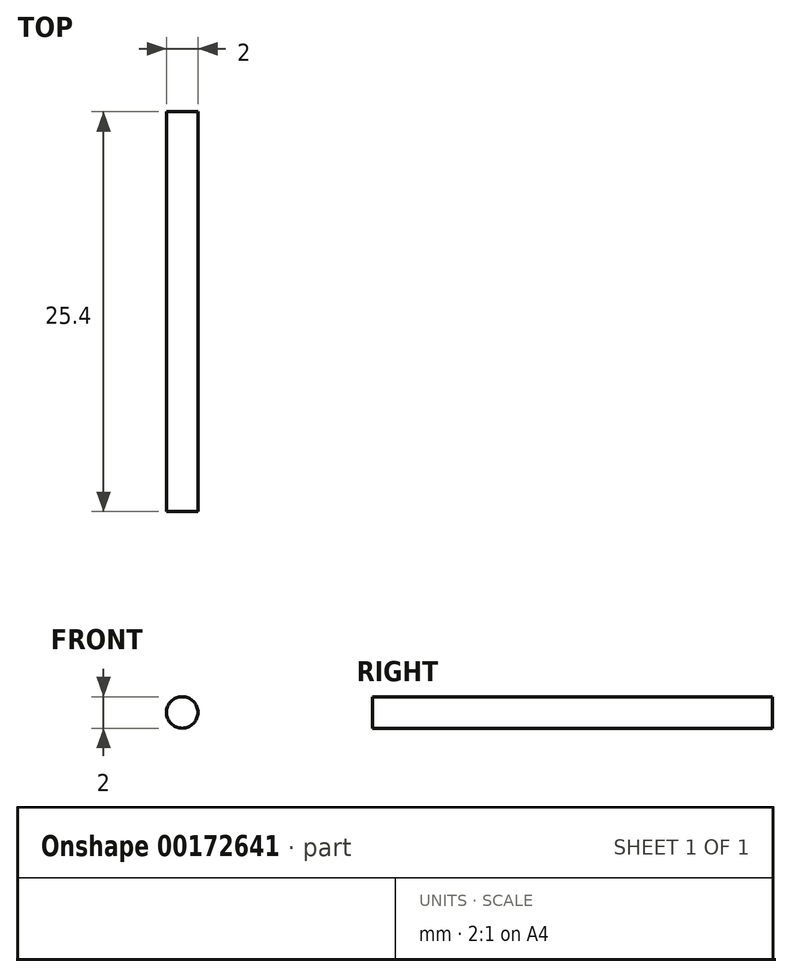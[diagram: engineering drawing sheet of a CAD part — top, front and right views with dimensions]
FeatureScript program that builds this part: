
annotation { "Feature Type Name" : "Feature", "Feature Type Description" : "" }
export const myFeature = defineFeature(function(context is Context, id is Id, definition is map)
    precondition{}
    {
        {
            var Q0;
            Q0=qCreatedBy(makeId("Front.planeOp"),FACE);
            var sketch = newSketch(context, id + "F0", { "sketchPlane" : qUnion([Q0])});
            skCircle(sketch, "E0", {"center": v(0, 0) * mm, "radius": 1 * mm});
            skSolve(sketch);
        }
        {
            var Q0;
            Q0 = qSketchRegion(id + "F0", true);
            extrude(context, id + "F1", {"entities" : qUnion([Q0]), "depth" : 25.4 * mm});
        }
    });
